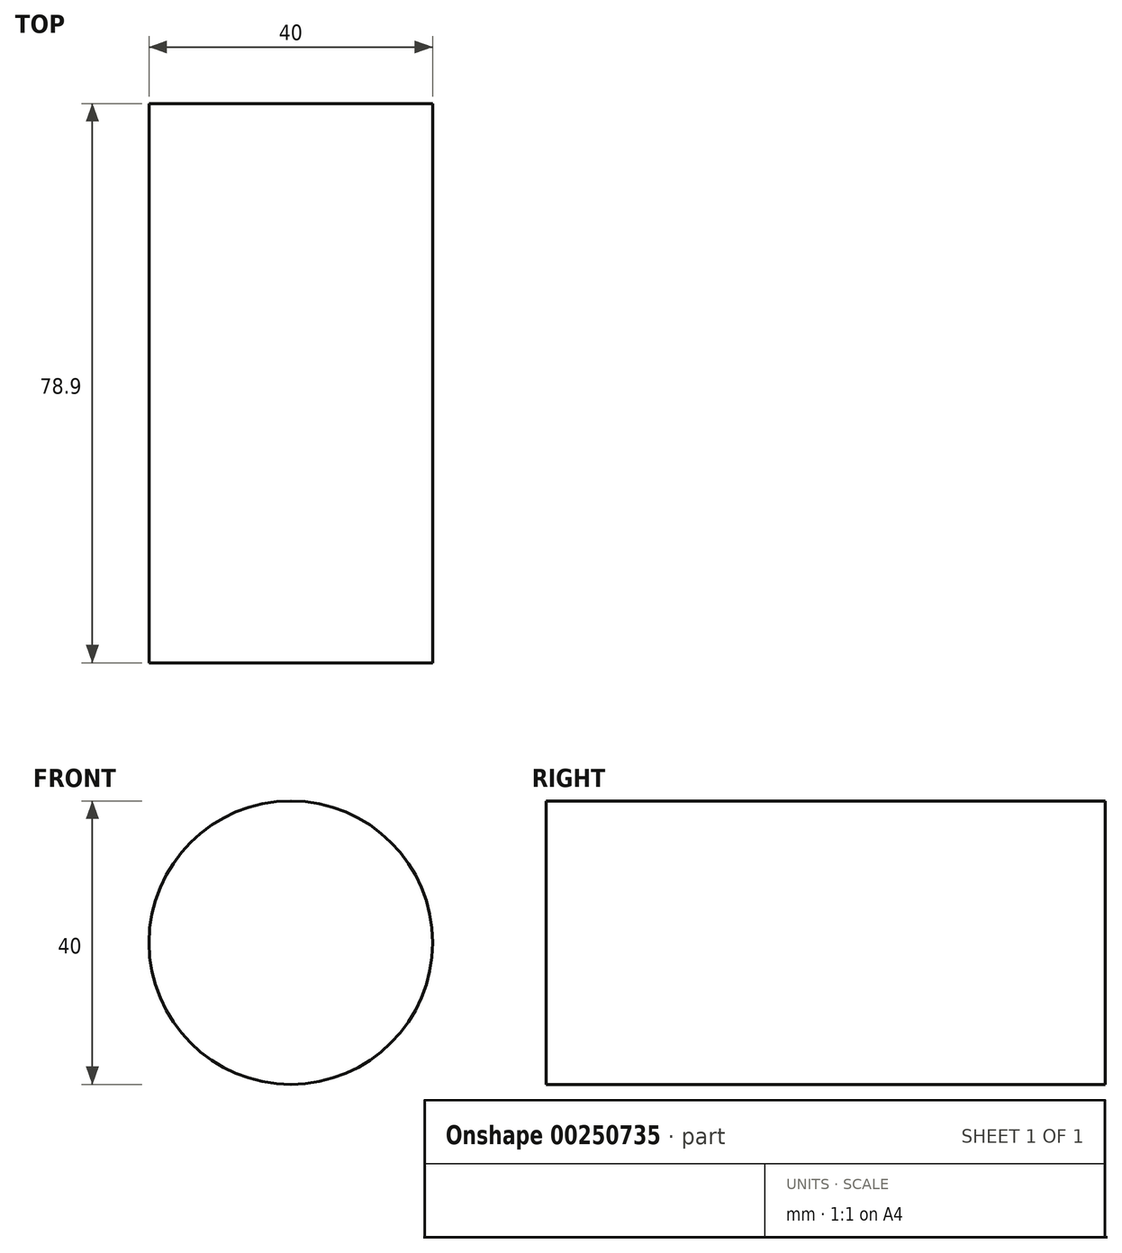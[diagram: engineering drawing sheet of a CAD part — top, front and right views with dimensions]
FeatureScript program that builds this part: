
annotation { "Feature Type Name" : "Feature", "Feature Type Description" : "" }
export const myFeature = defineFeature(function(context is Context, id is Id, definition is map)
    precondition{}
    {
        {
            var Q0;
            Q0=qCreatedBy(makeId("Front.planeOp"),FACE);
            var sketch = newSketch(context, id + "F0", { "sketchPlane" : qUnion([Q0])});
            skCircle(sketch, "E0", {"center": v(0, 0) * mm, "radius": 20 * mm});
            skSolve(sketch);
        }
        {
            var Q0;
            Q0=makeQuery(id+"F0.imprint","IMPRINT",FACE,{"disambiguationData":[TD([[makeQuery(id+"F0.imprint","IMPRINT",EDGE,{"derivedFrom":sQuery(id+"F0.wireOp",EDGE,"E0")}),1.0]])]});
            extrude(context, id + "F1", {"entities" : qUnion([Q0]), "depth" : 78.9 * mm});
        }
    });
